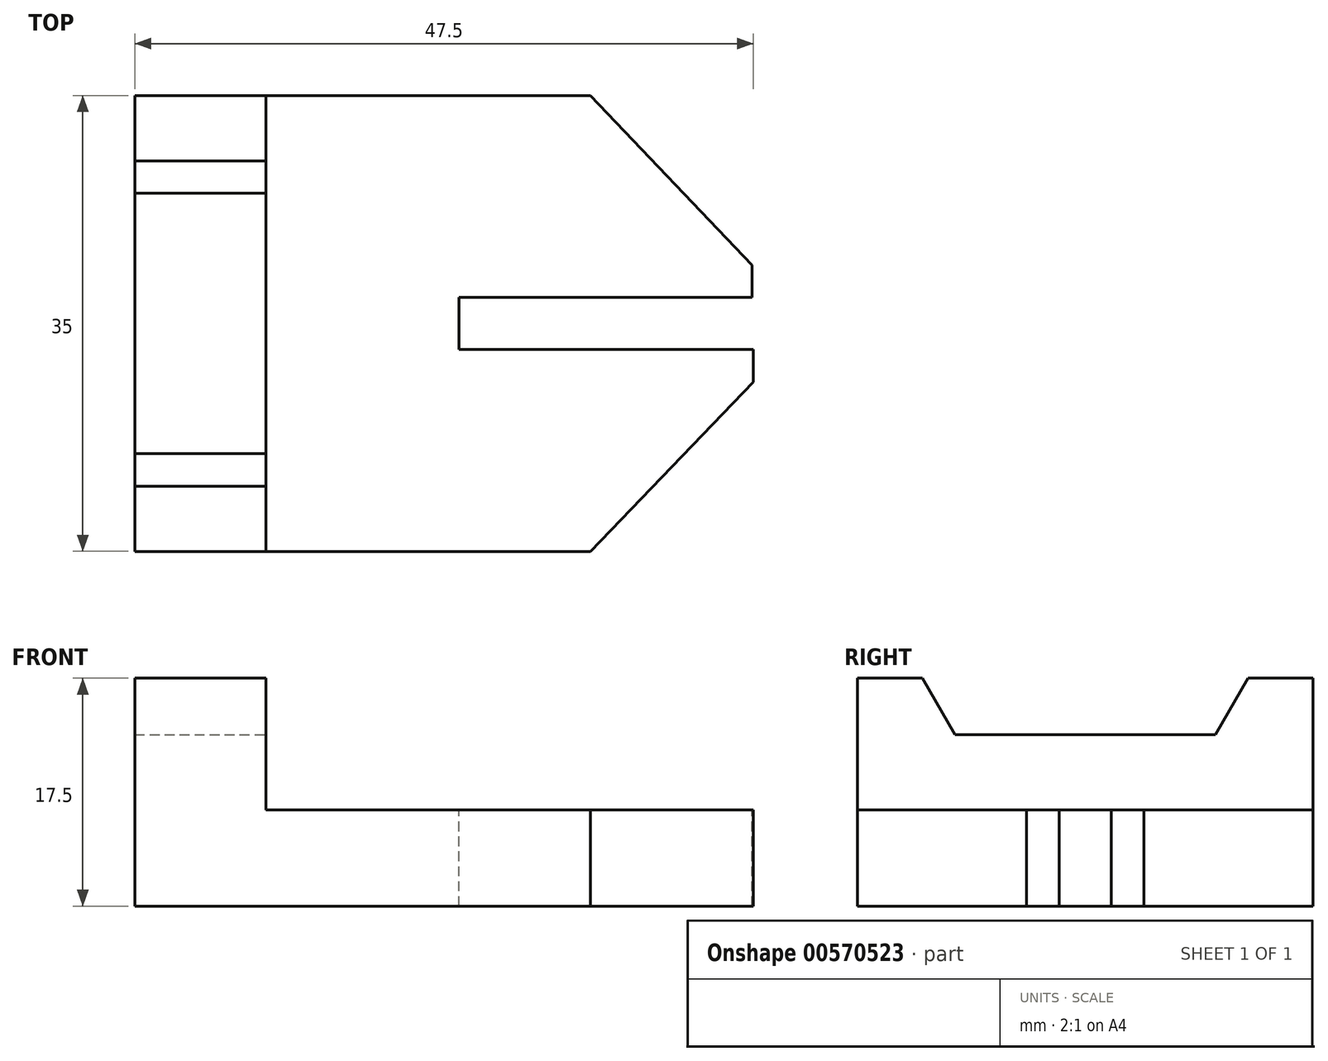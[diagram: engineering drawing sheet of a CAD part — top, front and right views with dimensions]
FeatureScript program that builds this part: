
annotation { "Feature Type Name" : "Feature", "Feature Type Description" : "" }
export const myFeature = defineFeature(function(context is Context, id is Id, definition is map)
    precondition{}
    {
        {
            var Q0;
            Q0=qCreatedBy(makeId("Top.planeOp"),FACE);
            var sketch = newSketch(context, id + "F0", { "sketchPlane" : qUnion([Q0])});
            skLineSegment(sketch, "E0.bottom", {"start": v(-47.4, 14.54) * mm, "end": v(0.1, 14.54) * mm});
            skLineSegment(sketch, "E0.top", {"start": v(-47.4, -20.46) * mm, "end": v(0.1, -20.46) * mm});
            skLineSegment(sketch, "E0.left", {"start": v(-47.4, 14.54) * mm, "end": v(-47.4, -20.46) * mm});
            skLineSegment(sketch, "E0.right", {"start": v(0.1, 14.54) * mm, "end": v(0.1, -20.46) * mm});
            skSolve(sketch);
        }
        {
            var Q0;
            Q0 = qSketchRegion(id + "F0", true);
            extrude(context, id + "F1", {"entities" : qUnion([Q0]), "depth" : 17.5 * mm, "offsetDistance" : 25 * mm});
        }
        {
            var Q0;
            Q0=makeQuery(id+"F1.opExtrude","SWEPT_FACE",FACE,{"disambiguationData":[OSD([sQuery(id+"F0.wireOp",EDGE,"E0.top")])]});
            var sketch = newSketch(context, id + "F2", { "sketchPlane" : qUnion([Q0])});
            skLineSegment(sketch, "E1", {"start": v(-47.4, 17.5) * mm, "end": v(-37.32, 17.5) * mm});
            skLineSegment(sketch, "E2", {"start": v(-37.32, 17.5) * mm, "end": v(-37.32, 7.38) * mm});
            skLineSegment(sketch, "E3", {"start": v(-37.32, 7.38) * mm, "end": v(0.1, 7.38) * mm});
            skSolve(sketch);
        }
        {
            var Q0;
            Q0 = qSketchRegion(id + "F2", true);
            var Q1;
            {var subQ0=sQuery(id+"F2.wireOp",EDGE,"E2");Q1=makeQuery(id+"F2.imprint","IMPRINT",FACE,{"disambiguationData":[TD([[makeQuery(id+"F2.imprint","IMPRINT",EDGE,{"derivedFrom":subQ0}),1.0]])]});}
            extrude(context, id + "F3", {"entities" : qUnion([Q0, Q1]), "operationType" : NewBodyOperationType.REMOVE, "endBound" : BoundingType.THROUGH_ALL, "oppositeDirection" : true, "depth" : 25 * mm, "offsetDistance" : 25 * mm});
        }
        {
            var Q0;
            Q0=makeQuery(id+"F3.boolean.opBoolean","COPY",FACE,{"derivedFrom":makeQuery(id+"F3.opExtrude","SWEPT_FACE",FACE,{"disambiguationData":[OSD([sQuery(id+"F2.wireOp",EDGE,"E2")])]})});
            var sketch = newSketch(context, id + "F4", { "sketchPlane" : qUnion([Q0])});
            skLineSegment(sketch, "E4", {"start": v(-20.46, 17.5) * mm, "end": v(-15.46, 17.5) * mm});
            skLineSegment(sketch, "E5", {"start": v(-15.46, 17.5) * mm, "end": v(-12.96, 13.17) * mm});
            skLineSegment(sketch, "E6", {"start": v(-12.96, 13.17) * mm, "end": v(7.04, 13.17) * mm});
            skLineSegment(sketch, "E7", {"start": v(7.04, 13.17) * mm, "end": v(9.54, 17.5) * mm});
            skLineSegment(sketch, "E8", {"start": v(9.54, 17.5) * mm, "end": v(14.54, 17.5) * mm});
            skSolve(sketch);
        }
        {
            var Q0;
            Q0 = qSketchRegion(id + "F4", true);
            var Q1;
            {var subQ0=sQuery(id+"F4.wireOp",EDGE,"E5");Q1=makeQuery(id+"F4.imprint","IMPRINT",FACE,{"disambiguationData":[TD([[makeQuery(id+"F4.imprint","IMPRINT",EDGE,{"derivedFrom":subQ0}),1.0]])]});}
            extrude(context, id + "F5", {"entities" : qUnion([Q0, Q1]), "operationType" : NewBodyOperationType.REMOVE, "endBound" : BoundingType.THROUGH_ALL, "oppositeDirection" : true, "depth" : 25 * mm, "offsetDistance" : 25 * mm});
        }
        {
            var Q0;
            Q0=makeQuery(id+"F3.boolean.opBoolean","COPY",FACE,{"derivedFrom":makeQuery(id+"F3.opExtrude","SWEPT_FACE",FACE,{"disambiguationData":[OSD([sQuery(id+"F2.wireOp",EDGE,"E3")])]})});
            var sketch = newSketch(context, id + "F6", { "sketchPlane" : qUnion([Q0])});
            skLineSegment(sketch, "E9", {"start": v(0.1, -4.96) * mm, "end": v(-22.5, -4.96) * mm});
            skLineSegment(sketch, "E10", {"start": v(-22.5, -4.96) * mm, "end": v(-22.5, -0.96) * mm});
            skLineSegment(sketch, "E11", {"start": v(-22.5, -0.96) * mm, "end": v(0, -0.96) * mm});
            skLineSegment(sketch, "E12", {"start": v(0, -0.96) * mm, "end": v(0.1, 14.54) * mm});
            skSolve(sketch);
        }
        {
            var Q0;
            Q0 = qSketchRegion(id + "F6", true);
            var Q1;
            {var subQ1=sQuery(id+"F6.wireOp",EDGE,"E9");Q1=makeQuery(id+"F6.imprint","IMPRINT",FACE,{"disambiguationData":[TD([[makeQuery(id+"F6.imprint","IMPRINT",EDGE,{"derivedFrom":subQ1}),-1.0]])]});}
            extrude(context, id + "F7", {"entities" : qUnion([Q0, Q1]), "operationType" : NewBodyOperationType.REMOVE, "endBound" : BoundingType.THROUGH_ALL, "oppositeDirection" : true, "depth" : 25 * mm, "offsetDistance" : 25 * mm});
        }
        {
            var Q0;
            Q0=makeQuery(id+"F3.boolean.opBoolean","COPY",FACE,{"derivedFrom":makeQuery(id+"F3.opExtrude","SWEPT_FACE",FACE,{"disambiguationData":[OSD([sQuery(id+"F2.wireOp",EDGE,"E3")])]})});
            var sketch = newSketch(context, id + "F8", { "sketchPlane" : qUnion([Q0])});
            skLineSegment(sketch, "E13", {"start": v(0.1, -4.96) * mm, "end": v(0.1, -7.46) * mm});
            skLineSegment(sketch, "E14", {"start": v(0, -0.96) * mm, "end": v(0.02, 1.54) * mm});
            skLineSegment(sketch, "E15", {"start": v(0.1, -20.46) * mm, "end": v(-12.4, -20.46) * mm});
            skLineSegment(sketch, "E16", {"start": v(0.1, -9.72) * mm, "end": v(0.1, -7.46) * mm});
            skLineSegment(sketch, "E17", {"start": v(0.1, -7.46) * mm, "end": v(0.1, -9.72) * mm});
            skLineSegment(sketch, "E18", {"start": v(-12.4, -20.46) * mm, "end": v(0.1, -7.46) * mm});
            skLineSegment(sketch, "E19", {"start": v(0.02, 1.54) * mm, "end": v(-12.4, 14.54) * mm});
            skSolve(sketch);
        }
        {
            var Q0;
            Q0 = qSketchRegion(id + "F8", true);
            var Q1;
            {var subQ0=sQuery(id+"F8.wireOp",EDGE,"E15");Q1=makeQuery(id+"F8.imprint","IMPRINT",FACE,{"disambiguationData":[TD([[makeQuery(id+"F8.imprint","IMPRINT",EDGE,{"derivedFrom":subQ0}),1.0]])]});}
            var Q2;
            {var subQ0=sQuery(id+"F8.wireOp",EDGE,"E19");Q2=makeQuery(id+"F8.imprint","IMPRINT",FACE,{"disambiguationData":[TD([[makeQuery(id+"F8.imprint","IMPRINT",EDGE,{"derivedFrom":subQ0}),-1.0]])]});}
            extrude(context, id + "F9", {"entities" : qUnion([Q0, Q1, Q2]), "operationType" : NewBodyOperationType.REMOVE, "endBound" : BoundingType.THROUGH_ALL, "oppositeDirection" : true, "depth" : 25 * mm, "offsetDistance" : 25 * mm});
        }
    });
